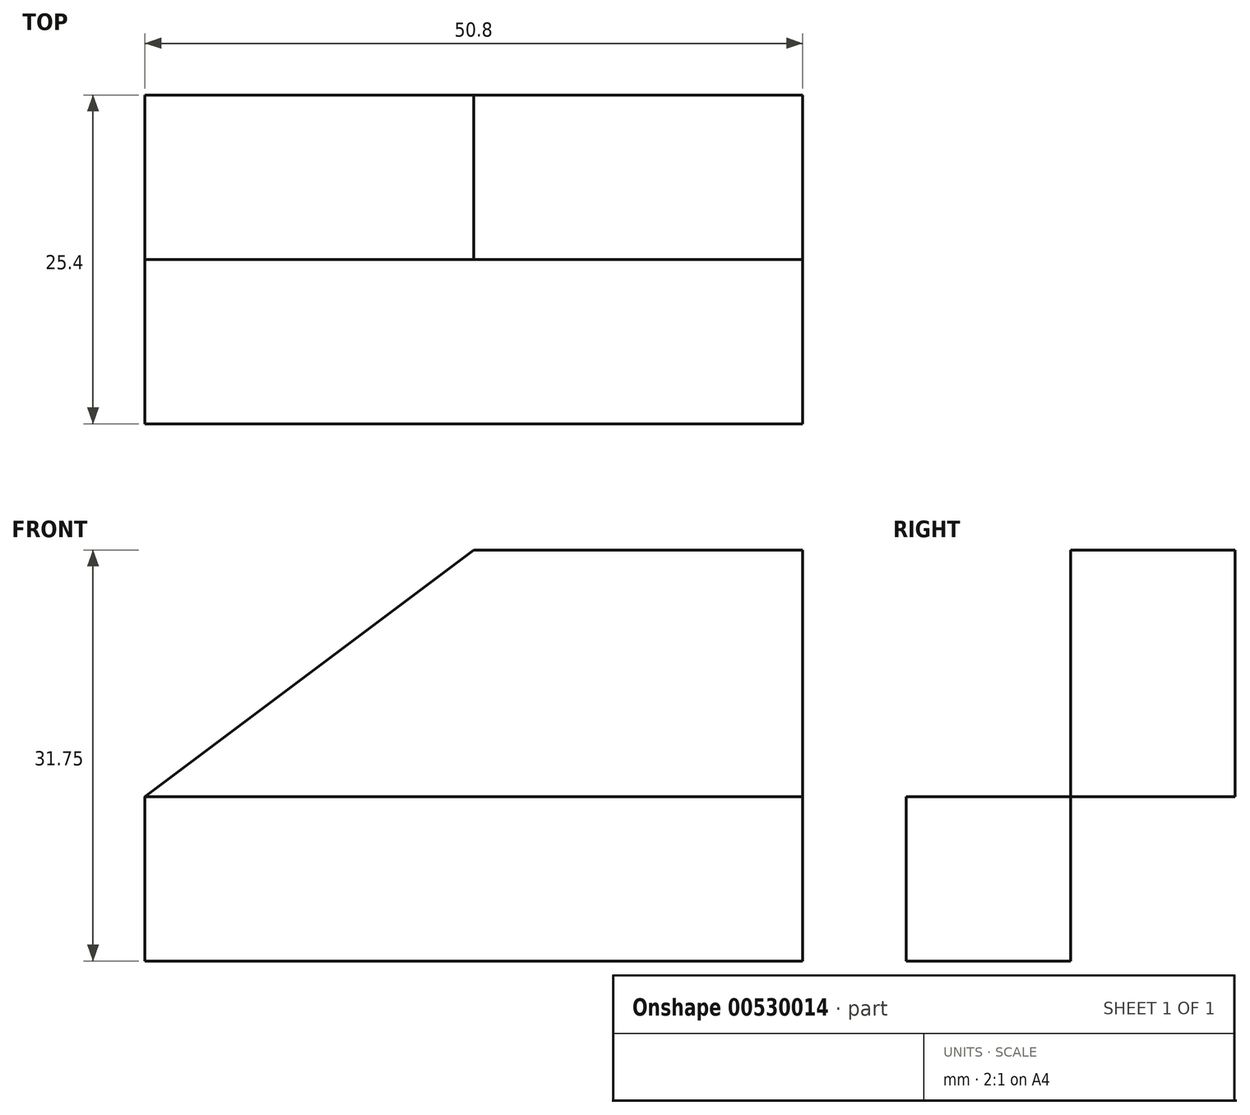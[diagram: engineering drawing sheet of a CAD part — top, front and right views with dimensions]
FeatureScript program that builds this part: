
annotation { "Feature Type Name" : "Feature", "Feature Type Description" : "" }
export const myFeature = defineFeature(function(context is Context, id is Id, definition is map)
    precondition{}
    {
        {
            var Q0;
            Q0=qCreatedBy(makeId("Right.planeOp"),FACE);
            var sketch = newSketch(context, id + "F0", { "sketchPlane" : qUnion([Q0])});
            skLineSegment(sketch, "E0", {"start": v(-44.77, 38.67) * mm, "end": v(-44.77, 25.97) * mm});
            skLineSegment(sketch, "E1", {"start": v(-44.77, 38.67) * mm, "end": v(-32.07, 38.67) * mm});
            skLineSegment(sketch, "E2", {"start": v(-44.77, 25.97) * mm, "end": v(-32.07, 25.97) * mm});
            skLineSegment(sketch, "E3", {"start": v(-32.07, 38.67) * mm, "end": v(-32.07, 25.97) * mm});
            skSolve(sketch);
        }
        {
            var Q0;
            Q0=makeQuery(id+"F0.imprint","IMPRINT",FACE,{"disambiguationData":[TD([[makeQuery(id+"F0.imprint","IMPRINT",EDGE,{"derivedFrom":sQuery(id+"F0.wireOp",EDGE,"E0")}),1.0]])]});
            extrude(context, id + "F1", {"entities" : qUnion([Q0]), "depth" : 50.8 * mm, "offsetDistance" : 25.4 * mm});
        }
        {
            var Q0;
            Q0=makeQuery(id+"F1.opExtrude","SWEPT_FACE",FACE,{"disambiguationData":[OSD([sQuery(id+"F0.wireOp",EDGE,"E3")])]});
            var sketch = newSketch(context, id + "F2", { "sketchPlane" : qUnion([Q0])});
            skLineSegment(sketch, "E4", {"start": v(-50.8, 38.67) * mm, "end": v(-50.8, 57.72) * mm});
            skLineSegment(sketch, "E5", {"start": v(-50.8, 57.72) * mm, "end": v(-25.4, 57.72) * mm});
            skLineSegment(sketch, "E6", {"start": v(-25.4, 57.72) * mm, "end": v(0, 38.67) * mm});
            skSolve(sketch);
        }
        {
            var Q0;
            Q0=makeQuery(id+"F2.imprint","IMPRINT",FACE,{"disambiguationData":[TD([[makeQuery(id+"F2.imprint","IMPRINT",EDGE,{"derivedFrom":sQuery(id+"F2.wireOp",EDGE,"E4")}),-1.0]])]});
            extrude(context, id + "F3", {"entities" : qUnion([Q0]), "depth" : 12.7 * mm, "offsetDistance" : 25.4 * mm});
        }
    });
